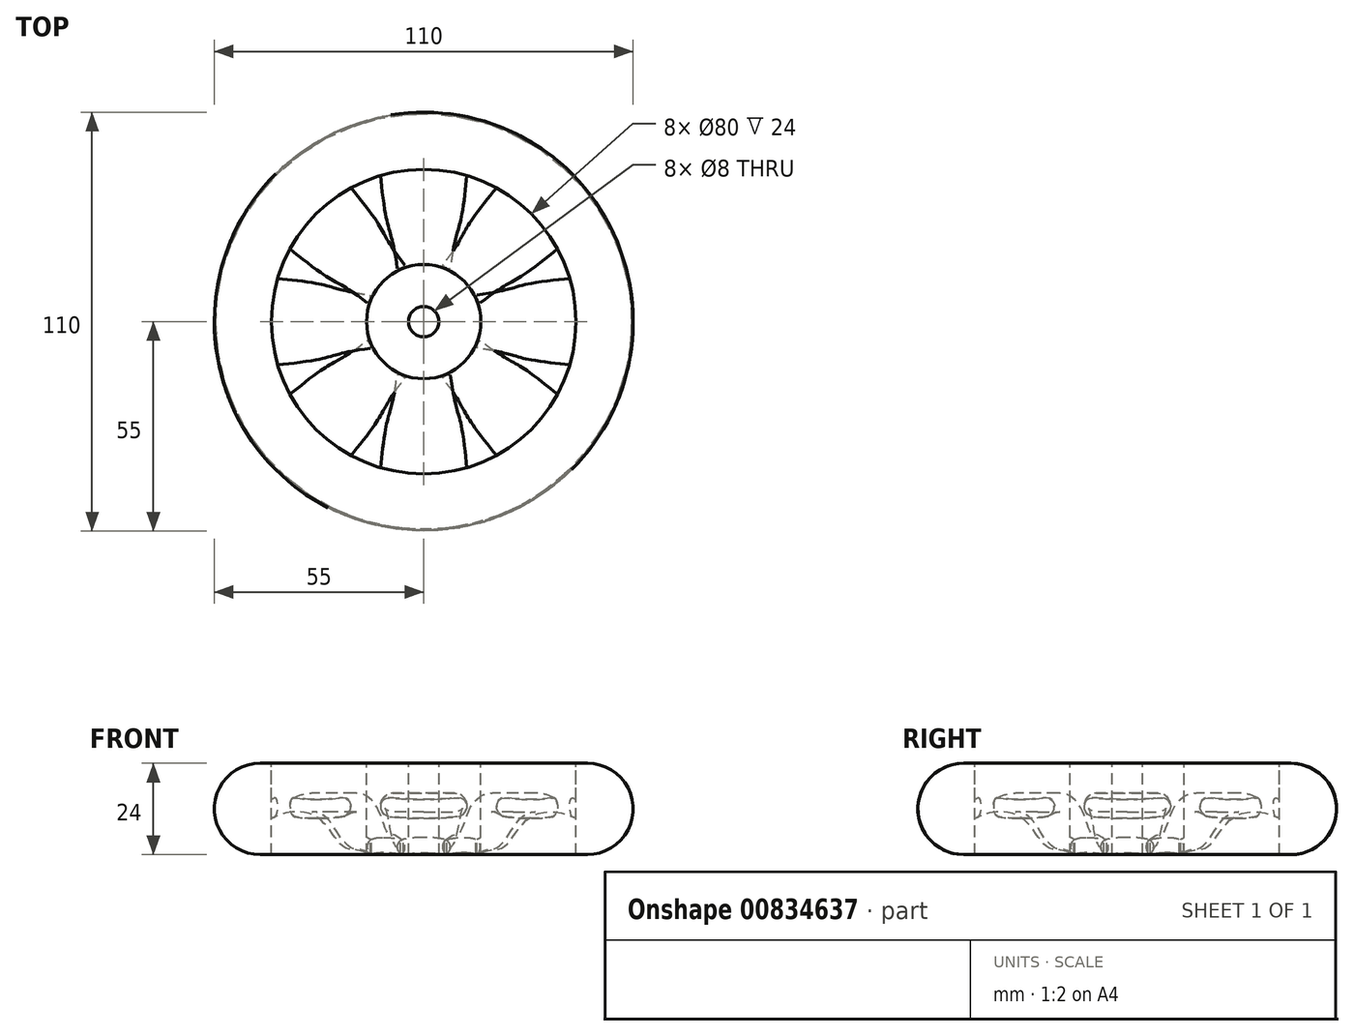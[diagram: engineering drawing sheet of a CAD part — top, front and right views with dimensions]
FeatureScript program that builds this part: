
annotation { "Feature Type Name" : "Feature", "Feature Type Description" : "" }
export const myFeature = defineFeature(function(context is Context, id is Id, definition is map)
    precondition{}
    {
        {
            var Q0;
            Q0=qCreatedBy(makeId("Top.planeOp"),FACE);
            var sketch = newSketch(context, id + "F0", { "sketchPlane" : qUnion([Q0])});
            skCircle(sketch, "E0", {"center": v(0, 0) * mm, "radius": 40 * mm});
            skSolve(sketch);
        }
        {
            var Q0;
            Q0=qCreatedBy(makeId("Front.planeOp"),FACE);
            var sketch = newSketch(context, id + "F1", { "sketchPlane" : qUnion([Q0])});
            skArc(sketch, "E1", {"start": v(-43, 12) * mm, "mid": v(-55, 0) * mm, "end": v(-43, -12) * mm});
            skLineSegment(sketch, "E2", {"start": v(-43, 12) * mm, "end": v(-40, 12) * mm});
            skLineSegment(sketch, "E3", {"start": v(-43, -12) * mm, "end": v(-40, -12) * mm});
            skLineSegment(sketch, "E4", {"start": v(-40, 12) * mm, "end": v(-40, -12) * mm});
            skSolve(sketch);
        }
        {
            var Q0;
            Q0=qSketchRegion(id+"F1",true);
            var Q1;
            Q1=qConstructionFilter(qBodyType(qCreatedBy(id+"F0",EDGE),BodyType.WIRE),ConstructionObject.NO);
            sweep(context, id + "F2", {"profiles" : qUnion([Q0]), "path" : qUnion([Q1])});
        }
        {
            var Q0;
            Q0=qCreatedBy(makeId("Right.planeOp"),FACE);
            cPlane(context, id + "F3", {"entities" : qUnion([Q0]), "cplaneType" : CPlaneType.OFFSET, "offset" : 40 * mm, "width" : 150 * mm, "height" : 150 * mm});
        }
        {
            var Q0;
            Q0=qCreatedBy(id+"F3.planeOp",FACE);
            var sketch = newSketch(context, id + "F4", { "sketchPlane" : qUnion([Q0])});
            skLineSegment(sketch, "E5", {"start": v(-9, 0) * mm, "end": v(9, 0) * mm});
            skArc(sketch, "E6.0.startCap", {"start": v(-9, -2.5) * mm, "mid": v(-11.5, 0) * mm, "end": v(-9, 2.5) * mm});
            skArc(sketch, "E6.0.endCap", {"start": v(9, 2.5) * mm, "mid": v(11.5, 0) * mm, "end": v(9, -2.5) * mm});
            skLineSegment(sketch, "E6.0.left", {"start": v(-9, 2.5) * mm, "end": v(9, 2.5) * mm});
            skLineSegment(sketch, "E6.0.right", {"start": v(-9, -2.5) * mm, "end": v(9, -2.5) * mm});
            skSolve(sketch);
        }
        {
            var Q0;
            Q0=qCreatedBy(makeId("Right.planeOp"),FACE);
            cPlane(context, id + "F5", {"entities" : qUnion([Q0]), "cplaneType" : CPlaneType.OFFSET, "offset" : 14 * mm, "width" : 150 * mm, "height" : 150 * mm});
        }
        {
            var Q0;
            Q0=qCreatedBy(id+"F5.planeOp",FACE);
            var sketch = newSketch(context, id + "F6", { "sketchPlane" : qUnion([Q0])});
            skLineSegment(sketch, "E7", {"start": v(-5, -10) * mm, "end": v(5, -10) * mm});
            skArc(sketch, "E8.0.startCap", {"start": v(-5, -12) * mm, "mid": v(-7, -10) * mm, "end": v(-5, -8) * mm});
            skArc(sketch, "E8.0.endCap", {"start": v(5, -8) * mm, "mid": v(7, -10) * mm, "end": v(5, -12) * mm});
            skLineSegment(sketch, "E8.0.left", {"start": v(-5, -8) * mm, "end": v(5, -8) * mm});
            skLineSegment(sketch, "E8.0.right", {"start": v(-5, -12) * mm, "end": v(5, -12) * mm});
            skSolve(sketch);
        }
        {
            var Q0;
            Q0=qCreatedBy(makeId("Front.planeOp"),FACE);
            var sketch = newSketch(context, id + "F7", { "sketchPlane" : qUnion([Q0])});
            skFitSpline(sketch, "E9", {"points": [v(14, -12) * mm, v(20.44, -10.27) * mm, v(24.06, -6.43) * mm, v(28.41, -1.97) * mm, v(40, -2.5) * mm], "startDerivative": vector(37.83, 21.17) * mm, "endDerivative": vector(47.32, -23.74) * mm});
            skSolve(sketch);
        }
        {
            var Q1;
            Q1=qSketchRegion(id+"F6",true);
            var Q2;
            Q2=qSketchRegion(id+"F4",true);
            var Q3;
            Q3=qConstructionFilter(qBodyType(qCreatedBy(id+"F7",EDGE),BodyType.WIRE),ConstructionObject.NO);
            loft(context, id + "F8", {"operationType" : NewBodyOperationType.ADD, "addGuides" : true, "sheetProfilesArray" : [{ "sheetProfileEntities" : qUnion([Q1]) }, { "sheetProfileEntities" : qUnion([Q2]) }], "guidesArray" : [{ "guideEntities" : qUnion([Q3]), "guideDerivativeType" : LoftGuideDerivativeType.DEFAULT, "guideDerivativeMagnitude" : 1 }]});
        }
        {
            var Q0;
            Q0=qCreatedBy(makeId("Front.planeOp"),FACE);
            var sketch = newSketch(context, id + "F9", { "sketchPlane" : qUnion([Q0])});
            skLineSegment(sketch, "E10.bottom", {"start": v(0, 12) * mm, "end": v(15, 12) * mm});
            skLineSegment(sketch, "E10.top", {"start": v(0, -12) * mm, "end": v(15, -12) * mm});
            skLineSegment(sketch, "E10.left", {"start": v(0, 12) * mm, "end": v(0, -12) * mm});
            skLineSegment(sketch, "E10.right", {"start": v(15, 12) * mm, "end": v(15, -12) * mm});
            skSolve(sketch);
        }
        {
            var Q0;
            Q0=qSketchRegion(id+"F9",true);
            var Q1;
            Q1=sQuery(id+"F9.wireOp",EDGE,"E10.left");
            revolve(context, id + "F10", {"operationType" : NewBodyOperationType.ADD, "surfaceOperationType" : NewSurfaceOperationType.NEW, "entities" : qUnion([Q0]), "axis" : qUnion([Q1]), "revolveType" : RevolveType.FULL});
        }
        {
            var Q0;
            Q0=makeQuery(id+"F2.opSweep","SWEPT_BODY",BODY,{"disambiguationData":[OSD([sQuery(id+"F0.wireOp",EDGE,"E0"),sQuery(id+"F1.wireOp",EDGE,"E1"),sQuery(id+"F1.wireOp",EDGE,"E2"),sQuery(id+"F1.wireOp",EDGE,"E3"),sQuery(id+"F1.wireOp",EDGE,"E4")])]});
            var Q1;
            Q1=makeQuery(id+"F2.opSweep","SWEPT_FACE",FACE,{"disambiguationData":[OSD([sQuery(id+"F0.wireOp",EDGE,"E0"),sQuery(id+"F1.wireOp",EDGE,"E4")])]});
            circularPattern(context, id + "F11", {"entities" : qUnion([Q0]), "axis" : qUnion([Q1]), "angle" : 360 * degree, "instanceCount" : 8, "oppositeDirection" : true, "equalSpace" : true});
        }
        {
            var Q0;
            Q0=makeQuery(id+"F10.opRevolve","SWEPT_FACE",FACE,{"disambiguationData":[OSD([sQuery(id+"F9.wireOp",EDGE,"E10.bottom")])]});
            var sketch = newSketch(context, id + "F12", { "sketchPlane" : qUnion([Q0])});
            skPoint(sketch, "E11", {"position": v(0, 0) * mm});
            skSolve(sketch);
        }
        {
            var Q0;
            Q0=sQuery(id+"F12.wireOp",VERTEX,"E11");
            var Q1;
            Q1=makeQuery(id+"F2.opSweep","SWEPT_BODY",BODY,{"disambiguationData":[OSD([sQuery(id+"F0.wireOp",EDGE,"E0"),sQuery(id+"F1.wireOp",EDGE,"E1"),sQuery(id+"F1.wireOp",EDGE,"E2"),sQuery(id+"F1.wireOp",EDGE,"E3"),sQuery(id+"F1.wireOp",EDGE,"E4")])]});
            var Q2;
            Q2=makeQuery(id+"F11.opPattern","COPY",BODY,{"derivedFrom":makeQuery(id+"F2.opSweep","SWEPT_BODY",BODY,{"disambiguationData":[OSD([sQuery(id+"F0.wireOp",EDGE,"E0"),sQuery(id+"F1.wireOp",EDGE,"E1"),sQuery(id+"F1.wireOp",EDGE,"E2"),sQuery(id+"F1.wireOp",EDGE,"E3"),sQuery(id+"F1.wireOp",EDGE,"E4")])]}),"instanceName":"1"});
            var Q3;
            Q3=makeQuery(id+"F11.opPattern","COPY",BODY,{"derivedFrom":makeQuery(id+"F2.opSweep","SWEPT_BODY",BODY,{"disambiguationData":[OSD([sQuery(id+"F0.wireOp",EDGE,"E0"),sQuery(id+"F1.wireOp",EDGE,"E1"),sQuery(id+"F1.wireOp",EDGE,"E2"),sQuery(id+"F1.wireOp",EDGE,"E3"),sQuery(id+"F1.wireOp",EDGE,"E4")])]}),"instanceName":"2"});
            var Q4;
            Q4=makeQuery(id+"F11.opPattern","COPY",BODY,{"derivedFrom":makeQuery(id+"F2.opSweep","SWEPT_BODY",BODY,{"disambiguationData":[OSD([sQuery(id+"F0.wireOp",EDGE,"E0"),sQuery(id+"F1.wireOp",EDGE,"E1"),sQuery(id+"F1.wireOp",EDGE,"E2"),sQuery(id+"F1.wireOp",EDGE,"E3"),sQuery(id+"F1.wireOp",EDGE,"E4")])]}),"instanceName":"3"});
            var Q5;
            Q5=makeQuery(id+"F11.opPattern","COPY",BODY,{"derivedFrom":makeQuery(id+"F2.opSweep","SWEPT_BODY",BODY,{"disambiguationData":[OSD([sQuery(id+"F0.wireOp",EDGE,"E0"),sQuery(id+"F1.wireOp",EDGE,"E1"),sQuery(id+"F1.wireOp",EDGE,"E2"),sQuery(id+"F1.wireOp",EDGE,"E3"),sQuery(id+"F1.wireOp",EDGE,"E4")])]}),"instanceName":"4"});
            var Q6;
            Q6=makeQuery(id+"F11.opPattern","COPY",BODY,{"derivedFrom":makeQuery(id+"F2.opSweep","SWEPT_BODY",BODY,{"disambiguationData":[OSD([sQuery(id+"F0.wireOp",EDGE,"E0"),sQuery(id+"F1.wireOp",EDGE,"E1"),sQuery(id+"F1.wireOp",EDGE,"E2"),sQuery(id+"F1.wireOp",EDGE,"E3"),sQuery(id+"F1.wireOp",EDGE,"E4")])]}),"instanceName":"5"});
            var Q7;
            Q7=makeQuery(id+"F11.opPattern","COPY",BODY,{"derivedFrom":makeQuery(id+"F2.opSweep","SWEPT_BODY",BODY,{"disambiguationData":[OSD([sQuery(id+"F0.wireOp",EDGE,"E0"),sQuery(id+"F1.wireOp",EDGE,"E1"),sQuery(id+"F1.wireOp",EDGE,"E2"),sQuery(id+"F1.wireOp",EDGE,"E3"),sQuery(id+"F1.wireOp",EDGE,"E4")])]}),"instanceName":"6"});
            var Q8;
            Q8=makeQuery(id+"F11.opPattern","COPY",BODY,{"derivedFrom":makeQuery(id+"F2.opSweep","SWEPT_BODY",BODY,{"disambiguationData":[OSD([sQuery(id+"F0.wireOp",EDGE,"E0"),sQuery(id+"F1.wireOp",EDGE,"E1"),sQuery(id+"F1.wireOp",EDGE,"E2"),sQuery(id+"F1.wireOp",EDGE,"E3"),sQuery(id+"F1.wireOp",EDGE,"E4")])]}),"instanceName":"7"});
            hole(context, id + "F13", {"style" : HoleStyle.SIMPLE, "endStyle" : HoleEndStyle.THROUGH, "holeDiameter" : 8 * mm, "majorDiameter" : 5 * mm, "isTappedThrough" : true, "tappedDepth" : 12 * mm, "tapClearance" : 3, "locations" : qUnion([Q0]), "scope" : qUnion([Q1, Q2, Q3, Q4, Q5, Q6, Q7, Q8])});
        }
    });
